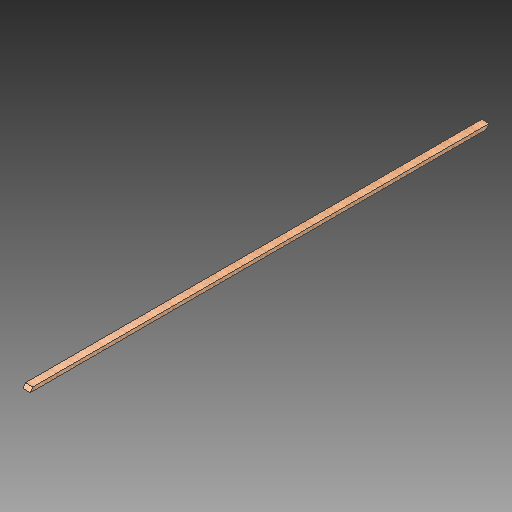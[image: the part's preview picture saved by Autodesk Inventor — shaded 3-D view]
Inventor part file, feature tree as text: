
AUTODESK INVENTOR PART (.ipt)
format: ipt  version: 2018 (Build 220112000, 112)  size: 267,776 bytes
history: native  units: mm
features: other x8, extrude x8, sketch x8, projected_geometry x7, fillet x4, reference x3
ambient origin geometry x8: Origin, YZ Plane, XZ Plane, XY Plane, X Axis, Y Axis, Z Axis, Center Point
bodies: Solid1 (feature_tree)
feature tree (38):
  parser-record x2  (decoder bookkeeping rows leaked as tree rows — omitted from the tree; the rows remain in map.json)
  extrude  "brædt"  Depth=80.0mm
  extrude  "spor til stål-håndfang"  Depth=40.0mm
  extrude  "spor til LED og liste"  Depth=4844.551mm
  extrude  "spor til ledninger"  Depth=5.0mm TaperAngle=0.0deg
  extrude  "endeafskær top"  Depth=6.3mm
  extrude  "endeafskær bund"  Depth=12.0mm TaperAngle=0.0deg
  fillet  "Fillet2"  Radius=1.0mm
  fillet  "Fillet3"  Radius=1.0mm
  fillet  "Fillet4"  Radius=10.0mm
  fillet  "Fillet5"  [1 undecoded]
  extrude  "pilothuller"  Depth=7.0mm TaperAngle=0.0deg
  extrude  "spor til acryl"  Depth=2.0mm
  sketch  "Sketch1"  dims[d5=5000.0mm d6=0.0mm d8=80.0mm]
  sketch  "Sketch2"  dims[d9=40.0mm d11=40.0mm]
  projected_geometry  "Projected Loop1"
  sketch  "Sketch3"  dims[d12=61.5mm d13=4844.551mm]
  projected_geometry  "Projected Loop2"
  sketch  "Sketch4"  dims[d14=3.0mm d15=5.0mm d16=0.0mm]
  projected_geometry  "Projected Loop3"
  sketch  "Sketch5"  dims[d17=9.5mm d18=6.3mm]
  projected_geometry  "Projected Loop4"
  sketch  "Sketch6"  dims[d19=12.0mm d20=12.0mm d21=0.0mm d22=1.0mm d23=1.0mm d24=10.0mm d25=0.0mm]
  projected_geometry  "Projected Loop5"
  sketch  "Sketch7"  dims[d26=0.0mm d27=7.0mm d28=0.0mm]
  reference  "Reference1"
  reference  "Reference2"
  reference  "Reference3"
  projected_geometry  "Projected Loop6"
  sketch  "Sketch8"  dims[d29=69.175mm d30=5.986479mm d31=7.0mm d32=0.0mm d33=5.986479mm d34=7.0mm d35=0.0mm d36=9.5mm d37=9.5mm d38=12.0mm d39=12.0mm d40=12.0mm d41=12.0mm d42=12.0mm d43=12.0mm d44=7.0mm d45=0.0mm d46=24.0mm d47=3.0mm d50=2.0mm d51=0.0mm d52=0.0mm d53=0.0mm]
  projected_geometry  "Projected Loop7"
  other  "søjle+vange.iam"
  other  "modul top:1"
  other  "stilladssøjle:1"
  other  "rør:1"
  other  "modul:1"
  other  "modul:2"
note: 1 required parameter value undecoded (feature->parameter linkage not recoverable at this tier; creation-order binding heuristic only, values carry confidence <= 0.55)
note: 2 file-system paths scrubbed to <path> (originals preserved in map.json)
